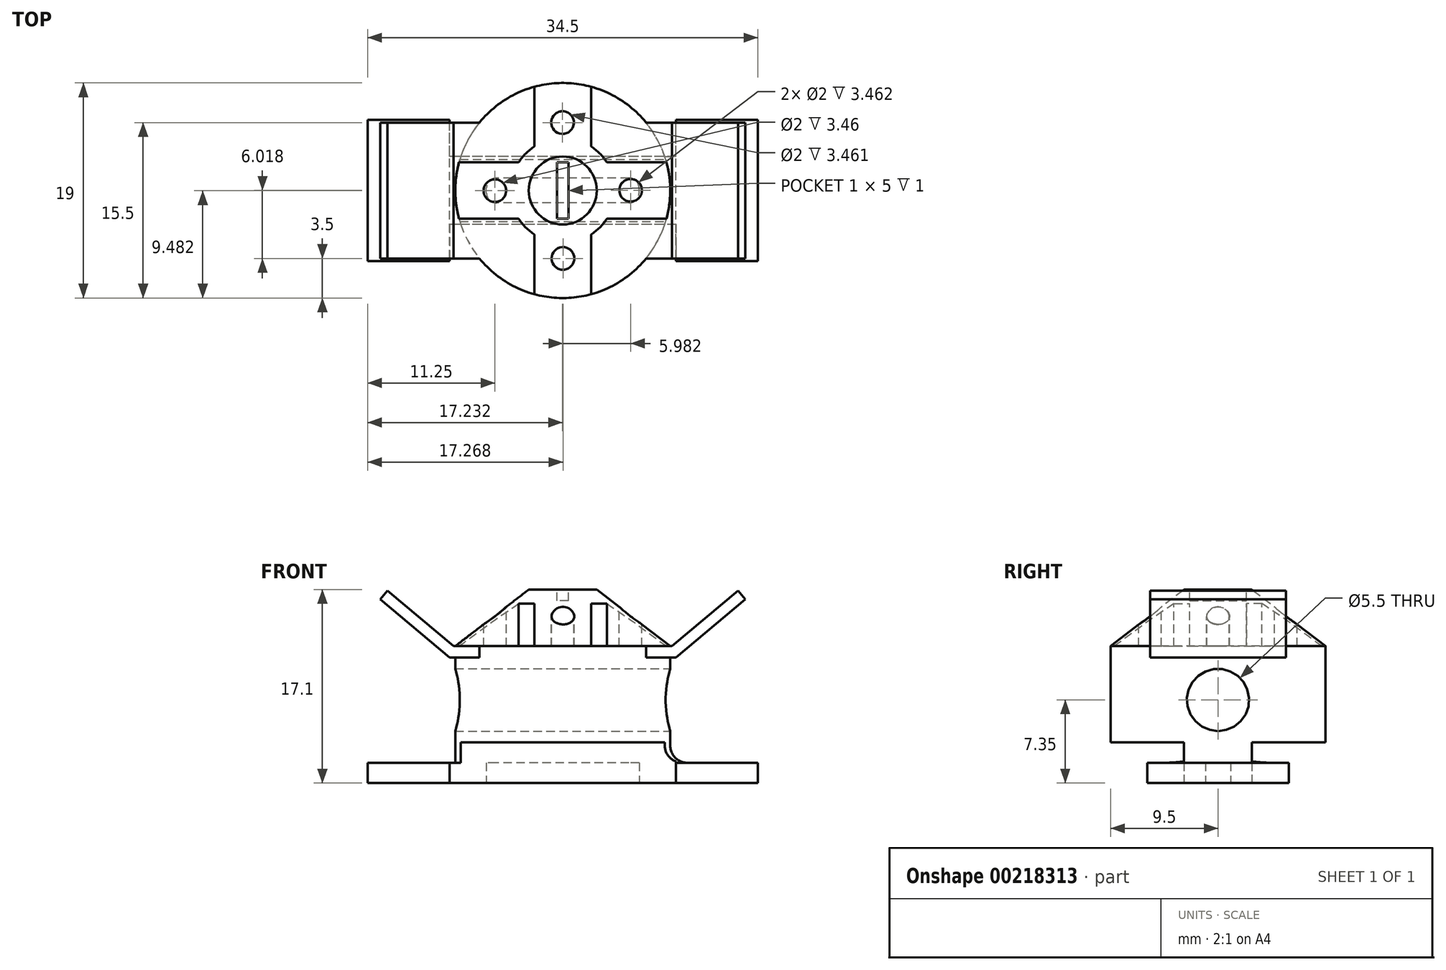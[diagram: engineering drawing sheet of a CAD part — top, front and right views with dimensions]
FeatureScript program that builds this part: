
annotation { "Feature Type Name" : "Feature", "Feature Type Description" : "" }
export const myFeature = defineFeature(function(context is Context, id is Id, definition is map)
    precondition{}
    {
        {
            var Q0;
            Q0=qCreatedBy(makeId("Top.planeOp"),FACE);
            var sketch = newSketch(context, id + "F0", { "sketchPlane" : qUnion([Q0])});
            skLineSegment(sketch, "E0.bottom", {"start": v(17.25, -6.25) * mm, "end": v(10, -6.25) * mm});
            skLineSegment(sketch, "E0.top", {"start": v(17.25, 6.25) * mm, "end": v(10, 6.25) * mm});
            skLineSegment(sketch, "E0.left", {"start": v(17.25, -6.25) * mm, "end": v(17.25, 6.25) * mm});
            skLineSegment(sketch, "E0.right", {"start": v(-17.25, -6.25) * mm, "end": v(-17.25, 6.25) * mm});
            skPoint(sketch, "E0.middle", {"position": v(0, 0) * mm});
            skLineSegment(sketch, "E1.bottom", {"start": v(10, -3) * mm, "end": v(-10, -3) * mm});
            skLineSegment(sketch, "E1.top", {"start": v(10, 3) * mm, "end": v(-10, 3) * mm});
            skLineSegment(sketch, "E2", {"start": v(-10, 3) * mm, "end": v(-10, 6.25) * mm});
            skLineSegment(sketch, "E3", {"start": v(-10, -3) * mm, "end": v(-10, -6.25) * mm});
            skLineSegment(sketch, "E4", {"start": v(10, 3) * mm, "end": v(10, 6.25) * mm});
            skLineSegment(sketch, "E5", {"start": v(10, -3) * mm, "end": v(10, -6.25) * mm});
            skLineSegment(sketch, "E6.trimOffspring", {"start": v(-10, 6.25) * mm, "end": v(-17.25, 6.25) * mm});
            skLineSegment(sketch, "E7.trimOffspring", {"start": v(-10, -6.25) * mm, "end": v(-17.25, -6.25) * mm});
            skLineSegment(sketch, "E8.bottom", {"start": v(5.85, -1.1) * mm, "end": v(-5.85, -1.1) * mm});
            skLineSegment(sketch, "E8.top", {"start": v(5.85, 1.1) * mm, "end": v(-5.85, 1.1) * mm});
            skLineSegment(sketch, "E8.left", {"start": v(6.75, -0.2) * mm, "end": v(6.75, 0.2) * mm});
            skLineSegment(sketch, "E8.right", {"start": v(-6.75, -0.2) * mm, "end": v(-6.75, 0.2) * mm});
            skPoint(sketch, "E9.visualSharp", {"position": v(-6.75, 1.1) * mm});
            skArc(sketch, "E9.filletArc", {"start": v(-5.85, 1.1) * mm, "mid": v(-6.49, 0.84) * mm, "end": v(-6.75, 0.2) * mm});
            skPoint(sketch, "E10.visualSharp", {"position": v(-6.75, -1.1) * mm});
            skArc(sketch, "E10.filletArc", {"start": v(-6.75, -0.2) * mm, "mid": v(-6.49, -0.84) * mm, "end": v(-5.85, -1.1) * mm});
            skPoint(sketch, "E11.visualSharp", {"position": v(6.75, 1.1) * mm});
            skArc(sketch, "E11.filletArc", {"start": v(6.75, 0.2) * mm, "mid": v(6.49, 0.84) * mm, "end": v(5.85, 1.1) * mm});
            skPoint(sketch, "E12.visualSharp", {"position": v(6.75, -1.1) * mm});
            skArc(sketch, "E12.filletArc", {"start": v(5.85, -1.1) * mm, "mid": v(6.49, -0.84) * mm, "end": v(6.75, -0.2) * mm});
            skLineSegment(sketch, "E13", {"start": v(-10, 3) * mm, "end": v(-10, -3) * mm});
            skLineSegment(sketch, "E14", {"start": v(10, 3) * mm, "end": v(10, -3) * mm});
            skSolve(sketch);
        }
        {
            var Q0;
            Q0 = qSketchRegion(id + "F0", true);
            extrude(context, id + "F1", {"entities" : qUnion([Q0]), "depth" : 1.8 * mm});
        }
        {
            var Q0;
            Q0=makeQuery(id+"F1.opExtrude","CAP_FACE",FACE,{"disambiguationData":[OSD([sQuery(id+"F0.wireOp",EDGE,"E0.bottom"),sQuery(id+"F0.wireOp",EDGE,"E0.top"),sQuery(id+"F0.wireOp",EDGE,"E0.left"),sQuery(id+"F0.wireOp",EDGE,"E0.right"),sQuery(id+"F0.wireOp",EDGE,"E1.bottom"),sQuery(id+"F0.wireOp",EDGE,"E1.top"),sQuery(id+"F0.wireOp",EDGE,"E2"),sQuery(id+"F0.wireOp",EDGE,"E3"),sQuery(id+"F0.wireOp",EDGE,"E4"),sQuery(id+"F0.wireOp",EDGE,"E5"),sQuery(id+"F0.wireOp",EDGE,"E6.trimOffspring"),sQuery(id+"F0.wireOp",EDGE,"E7.trimOffspring"),sQuery(id+"F0.wireOp",EDGE,"E8.bottom"),sQuery(id+"F0.wireOp",EDGE,"E8.top"),sQuery(id+"F0.wireOp",EDGE,"E9.filletArc"),sQuery(id+"F0.wireOp",EDGE,"E10.filletArc"),sQuery(id+"F0.wireOp",EDGE,"E11.filletArc"),sQuery(id+"F0.wireOp",EDGE,"E12.filletArc")])],"isStart":false});
            var sketch = newSketch(context, id + "F2", { "sketchPlane" : qUnion([Q0])});
            skPoint(sketch, "E15.middle", {"position": v(0, 0) * mm});
            skLineSegment(sketch, "E16.bottom", {"start": v(9.01, -3) * mm, "end": v(-9.01, -3) * mm});
            skLineSegment(sketch, "E16.top", {"start": v(9.01, 3) * mm, "end": v(-9.01, 3) * mm});
            skArc(sketch, "E17", {"start": v(-9.01, 3) * mm, "mid": v(-9.5, 0) * mm, "end": v(-9.01, -3) * mm});
            skPoint(sketch, "E18", {"position": v(-9.01, 3) * mm});
            skPoint(sketch, "E19", {"position": v(-9.01, -3) * mm});
            skPoint(sketch, "E20", {"position": v(9.01, -3) * mm});
            skPoint(sketch, "E21", {"position": v(9.01, 3) * mm});
            skPoint(sketch, "E16.right.end.orphan", {"position": v(-10, 3) * mm});
            skPoint(sketch, "E22.orphan", {"position": v(-10, -3) * mm});
            skArc(sketch, "E23.trimOffspring", {"start": v(9.01, -3) * mm, "mid": v(9.5, 0) * mm, "end": v(9.01, 3) * mm});
            skPoint(sketch, "E16.left.end.orphan", {"position": v(10, 3) * mm});
            skPoint(sketch, "E24.orphan", {"position": v(10, -3) * mm});
            skSolve(sketch);
        }
        {
            var Q0;
            Q0 = qSketchRegion(id + "F2", true);
            extrude(context, id + "F3", {"entities" : qUnion([Q0]), "operationType" : NewBodyOperationType.ADD, "depth" : 1.8 * mm});
        }
        {
            var Q0;
            Q0=makeQuery(id+"F3.opExtrude","CAP_EDGE",EDGE,{"disambiguationData":[OSD([sQuery(id+"F2.wireOp",EDGE,"E17")])],"isStart":true});
            var Q1;
            Q1=makeQuery(id+"F3.opExtrude","CAP_EDGE",EDGE,{"disambiguationData":[OSD([sQuery(id+"F2.wireOp",EDGE,"E23.trimOffspring")])],"isStart":true});
            fillet(context, id + "F4", {"entities" : qUnion([Q0, Q1]), "radius" : 1.5 * mm, "tangentPropagation" : true, "allowEdgeOverflow" : false});
        }
        {
            var Q0;
            Q0=makeQuery(id+"F3.opExtrude","CAP_FACE",FACE,{"disambiguationData":[OSD([sQuery(id+"F2.wireOp",EDGE,"E16.bottom"),sQuery(id+"F2.wireOp",EDGE,"E16.top"),sQuery(id+"F2.wireOp",EDGE,"E17"),sQuery(id+"F2.wireOp",EDGE,"E23.trimOffspring")])],"isStart":false});
            var sketch = newSketch(context, id + "F5", { "sketchPlane" : qUnion([Q0])});
            skCircle(sketch, "E25", {"center": v(0, 0) * mm, "radius": 9.5 * mm});
            skSolve(sketch);
        }
        {
            var Q0;
            Q0 = qSketchRegion(id + "F5", true);
            extrude(context, id + "F6", {"entities" : qUnion([Q0]), "operationType" : NewBodyOperationType.ADD, "depth" : 8.5 * mm});
        }
        {
            var Q0;
            Q0=makeQuery(id+"F6.opExtrude","CAP_FACE",FACE,{"disambiguationData":[OSD([sQuery(id+"F5.wireOp",EDGE,"E25")])],"isStart":false});
            var sketch = newSketch(context, id + "F7", { "sketchPlane" : qUnion([Q0])});
            skLineSegment(sketch, "E26.bottom", {"start": v(10, -6) * mm, "end": v(-10, -6) * mm});
            skLineSegment(sketch, "E26.top", {"start": v(10, 6) * mm, "end": v(-10, 6) * mm});
            skLineSegment(sketch, "E26.left", {"start": v(10, -6) * mm, "end": v(10, 6) * mm});
            skLineSegment(sketch, "E26.right", {"start": v(-10, -6) * mm, "end": v(-10, 6) * mm});
            skPoint(sketch, "E26.middle", {"position": v(0, 0) * mm});
            skPoint(sketch, "E27", {"position": v(-10, 6) * mm});
            skPoint(sketch, "E28", {"position": v(-10, -6) * mm});
            skPoint(sketch, "E29", {"position": v(10, -6) * mm});
            skPoint(sketch, "E30", {"position": v(10, 6) * mm});
            skLineSegment(sketch, "E31", {"start": v(0, 11) * mm, "end": v(0, -11.61) * mm, "construction": true});
            skPoint(sketch, "E31.startSnap0", {"position": v(0, 6) * mm});
            skSolve(sketch);
        }
        {
            var Q0;
            Q0 = qSketchRegion(id + "F7", true);
            extrude(context, id + "F8", {"entities" : qUnion([Q0]), "operationType" : NewBodyOperationType.ADD, "oppositeDirection" : true, "depth" : 1 * mm});
        }
        {
            var Q0;
            {var subQ0=sQuery(id+"F7.wireOp",EDGE,"E26.bottom");var subQ1=sQuery(id+"F7.wireOp",EDGE,"E26.right");Q0=makeQuery(id+"F8.boolean.opBoolean","SPLIT",EDGE,{"disambiguationData":[TD([makeQuery(id+"F8.opExtrude","SWEPT_FACE",FACE,{"disambiguationData":[OSD([subQ0])]})])],"derivedFrom":makeQuery(id+"F8.opExtrude","CAP_EDGE",EDGE,{"disambiguationData":[OSD([subQ1])],"isStart":false})});}
            cPlane(context, id + "F9", {"entities" : qUnion([Q0]), "cplaneType" : CPlaneType.LINE_ANGLE, "offset" : 25 * mm, "angle" : 40 * degree, "width" : 150 * mm, "height" : 150 * mm});
        }
        {
            var Q0;
            Q0=qCreatedBy(id+"F9.planeOp",FACE);
            var sketch = newSketch(context, id + "F10", { "sketchPlane" : qUnion([Q0])});
            skLineSegment(sketch, "E32.bottom", {"start": v(-14.8, 6) * mm, "end": v(-22.8, 6) * mm});
            skLineSegment(sketch, "E32.top", {"start": v(-14.8, -6) * mm, "end": v(-22.8, -6) * mm});
            skLineSegment(sketch, "E32.left", {"start": v(-14.8, 6) * mm, "end": v(-14.8, -6) * mm});
            skLineSegment(sketch, "E32.right", {"start": v(-22.8, 6) * mm, "end": v(-22.8, -6) * mm});
            skLineSegment(sketch, "E33.bottom", {"start": v(-14.8, 6) * mm, "end": v(-13.8, 6) * mm});
            skLineSegment(sketch, "E33.top", {"start": v(-14.8, -6) * mm, "end": v(-13.8, -6) * mm});
            skLineSegment(sketch, "E33.right", {"start": v(-13.8, 6) * mm, "end": v(-13.8, -6) * mm});
            skSolve(sketch);
        }
        {
            var Q0;
            Q0=makeQuery(id+"F10.imprint","IMPRINT",FACE,{"disambiguationData":[TD([[makeQuery(id+"F10.imprint","IMPRINT",EDGE,{"derivedFrom":sQuery(id+"F10.wireOp",EDGE,"E32.bottom")}),1.0]])]});
            extrude(context, id + "F11", {"entities" : qUnion([Q0]), "depth" : 1 * mm});
        }
        {
            var Q0;
            Q0=makeQuery(id+"F11.opExtrude","SWEPT_BODY",BODY,{"disambiguationData":[OSD([sQuery(id+"F10.wireOp",EDGE,"E32.bottom"),sQuery(id+"F10.wireOp",EDGE,"E32.top"),sQuery(id+"F10.wireOp",EDGE,"E32.right"),sQuery(id+"F10.wireOp",EDGE,"E32.left")])]});
            var Q1;
            Q1=qCreatedBy(makeId("Right.planeOp"),FACE);
            mirror(context, id + "F12", {"operationType" : NewBodyOperationType.ADD, "entities" : qUnion([Q0]), "mirrorPlane" : qUnion([Q1])});
        }
        {
            var Q0;
            Q0=qCreatedBy(makeId("Front.planeOp"),FACE);
            var sketch = newSketch(context, id + "F13", { "sketchPlane" : qUnion([Q0])});
            skLineSegment(sketch, "E34", {"start": v(0, 12.1) * mm, "end": v(0, 17.1) * mm});
            skLineSegment(sketch, "E35", {"start": v(0, 17.1) * mm, "end": v(-3, 17.1) * mm});
            skLineSegment(sketch, "E36", {"start": v(-3, 17.1) * mm, "end": v(-9.5, 12.1) * mm});
            skLineSegment(sketch, "E37", {"start": v(-9.5, 12.1) * mm, "end": v(0, 12.1) * mm});
            skSolve(sketch);
        }
        {
            var Q0;
            Q0 = qSketchRegion(id + "F13", true);
            var Q1;
            Q1=sQuery(id+"F13.wireOp",EDGE,"E34");
            revolve(context, id + "F14", {"operationType" : NewBodyOperationType.ADD, "entities" : qUnion([Q0]), "axis" : qUnion([Q1]), "revolveType" : RevolveType.FULL});
        }
        {
            var Q0;
            Q0=makeQuery(id+"F14.opRevolve","SWEPT_FACE",FACE,{"disambiguationData":[OSD([sQuery(id+"F13.wireOp",EDGE,"E35")])]});
            var sketch = newSketch(context, id + "F15", { "sketchPlane" : qUnion([Q0])});
            skArc(sketch, "E38", {"start": v(-2.5, 3.9) * mm, "mid": v(-3.27, 3.27) * mm, "end": v(-3.9, 2.5) * mm});
            skArc(sketch, "E39", {"start": v(-2.5, 9.17) * mm, "mid": v(-6.72, 6.72) * mm, "end": v(-9.17, 2.5) * mm});
            skLineSegment(sketch, "E40.left", {"start": v(2.5, -9.17) * mm, "end": v(2.5, -3.9) * mm});
            skLineSegment(sketch, "E40.right", {"start": v(-2.5, -9.5) * mm, "end": v(-2.5, -3.9) * mm});
            skLineSegment(sketch, "E41.bottom", {"start": v(9.17, -2.5) * mm, "end": v(3.9, -2.5) * mm});
            skLineSegment(sketch, "E41.top", {"start": v(9.17, 2.5) * mm, "end": v(3.9, 2.5) * mm});
            skLineSegment(sketch, "E42.trimOffspring", {"start": v(-2.5, 3.9) * mm, "end": v(-2.5, 9.17) * mm});
            skLineSegment(sketch, "E43.trimOffspring", {"start": v(-3.9, 2.5) * mm, "end": v(-9.17, 2.5) * mm});
            skArc(sketch, "E44.trimOffspring", {"start": v(-9.17, -2.5) * mm, "mid": v(-6.72, -6.72) * mm, "end": v(-2.5, -9.17) * mm});
            skPoint(sketch, "E45.orphan", {"position": v(-2.5, 9.5) * mm});
            skPoint(sketch, "E46.orphan", {"position": v(2.5, 9.5) * mm});
            skPoint(sketch, "E47.orphan", {"position": v(-9.5, 2.5) * mm});
            skPoint(sketch, "E48.orphan", {"position": v(-9.5, -2.5) * mm});
            skLineSegment(sketch, "E49.trimOffspring", {"start": v(-3.9, -2.5) * mm, "end": v(-9.17, -2.5) * mm});
            skArc(sketch, "E50.trimOffspring", {"start": v(-3.9, -2.5) * mm, "mid": v(-3.27, -3.27) * mm, "end": v(-2.5, -3.9) * mm});
            skLineSegment(sketch, "E51.trimOffspring", {"start": v(2.5, 3.9) * mm, "end": v(2.5, 9.17) * mm});
            skArc(sketch, "E52.trimOffspring", {"start": v(2.5, -3.9) * mm, "mid": v(3.27, -3.27) * mm, "end": v(3.9, -2.5) * mm});
            skArc(sketch, "E53.trimOffspring", {"start": v(3.9, 2.5) * mm, "mid": v(3.27, 3.27) * mm, "end": v(2.5, 3.9) * mm});
            skArc(sketch, "E54.trimOffspring", {"start": v(2.5, -9.17) * mm, "mid": v(6.72, -6.72) * mm, "end": v(9.17, -2.5) * mm});
            skPoint(sketch, "E55.orphan", {"position": v(2.5, -9.5) * mm});
            skPoint(sketch, "E56.orphan", {"position": v(9.5, 2.5) * mm});
            skArc(sketch, "E57.trimOffspring", {"start": v(9.17, 2.5) * mm, "mid": v(6.72, 6.72) * mm, "end": v(2.5, 9.17) * mm});
            skPoint(sketch, "E58.orphan", {"position": v(9.5, -2.5) * mm});
            skCircle(sketch, "E59", {"center": v(0, 0) * mm, "radius": 6 * mm, "construction": true});
            skLineSegment(sketch, "E60", {"start": v(-10.51, 0) * mm, "end": v(10.47, 0) * mm, "construction": true});
            skLineSegment(sketch, "E61", {"start": v(-0.02, -9.48) * mm, "end": v(-0.02, 7.04) * mm, "construction": true});
            skPoint(sketch, "E61.startSnap0", {"position": v(-0.02, 0) * mm});
            skPoint(sketch, "E62", {"position": v(-0.02, 6) * mm});
            skCircle(sketch, "E63", {"center": v(-0.02, 6) * mm, "radius": 1 * mm});
            skCircle(sketch, "E64.1.0", {"center": v(-6, -0.02) * mm, "radius": 1 * mm});
            skCircle(sketch, "E64.2.0", {"center": v(0.02, -6) * mm, "radius": 1 * mm});
            skCircle(sketch, "E64.3.0", {"center": v(6, 0.02) * mm, "radius": 1 * mm});
            skSolve(sketch);
        }
        {
            var Q0;
            Q0 = qSketchRegion(id + "F15", true);
            extrude(context, id + "F16", {"entities" : qUnion([Q0]), "operationType" : NewBodyOperationType.REMOVE, "oppositeDirection" : true, "depth" : 5 * mm});
        }
        {
            var Q0;
            Q0=makeQuery(id+"F14.opRevolve","SWEPT_FACE",FACE,{"disambiguationData":[OSD([sQuery(id+"F13.wireOp",EDGE,"E35")])]});
            var sketch = newSketch(context, id + "F17", { "sketchPlane" : qUnion([Q0])});
            skLineSegment(sketch, "E65.bottom", {"start": v(0.5, -2.5) * mm, "end": v(-0.5, -2.5) * mm});
            skLineSegment(sketch, "E65.top", {"start": v(0.5, 2.5) * mm, "end": v(-0.5, 2.5) * mm});
            skLineSegment(sketch, "E65.left", {"start": v(0.5, -2.5) * mm, "end": v(0.5, 2.5) * mm});
            skLineSegment(sketch, "E65.right", {"start": v(-0.5, -2.5) * mm, "end": v(-0.5, 2.5) * mm});
            skPoint(sketch, "E65.middle", {"position": v(0, 0) * mm});
            skSolve(sketch);
        }
        {
            var Q0;
            Q0 = qSketchRegion(id + "F17", true);
            extrude(context, id + "F18", {"entities" : qUnion([Q0]), "operationType" : NewBodyOperationType.REMOVE, "oppositeDirection" : true, "depth" : 1 * mm});
        }
        {
            var Q0;
            Q0=qCreatedBy(makeId("Right.planeOp"),FACE);
            cPlane(context, id + "F19", {"entities" : qUnion([Q0]), "cplaneType" : CPlaneType.OFFSET, "offset" : 20 * mm, "width" : 150 * mm, "height" : 150 * mm});
        }
        {
            var Q0;
            Q0=qCreatedBy(id+"F19.planeOp",FACE);
            var sketch = newSketch(context, id + "F20", { "sketchPlane" : qUnion([Q0])});
            skLineSegment(sketch, "E66", {"start": v(0, 0) * mm, "end": v(0, 22.9) * mm, "construction": true});
            skPoint(sketch, "E67", {"position": v(0, 3.6) * mm});
            skPoint(sketch, "E68", {"position": v(0, 11.1) * mm});
            skPoint(sketch, "E69", {"position": v(0, 7.35) * mm});
            skSolve(sketch);
        }
        {
            var Q0;
            Q0=sQuery(id+"F20.wireOp",VERTEX,"E69");
            var Q1;
            Q1=makeQuery(id+"F1.opExtrude","SWEPT_BODY",BODY,{"disambiguationData":[OSD([sQuery(id+"F0.wireOp",EDGE,"E0.bottom"),sQuery(id+"F0.wireOp",EDGE,"E0.top"),sQuery(id+"F0.wireOp",EDGE,"E0.left"),sQuery(id+"F0.wireOp",EDGE,"E0.right"),sQuery(id+"F0.wireOp",EDGE,"E1.bottom"),sQuery(id+"F0.wireOp",EDGE,"E1.top"),sQuery(id+"F0.wireOp",EDGE,"E2"),sQuery(id+"F0.wireOp",EDGE,"E3"),sQuery(id+"F0.wireOp",EDGE,"E4"),sQuery(id+"F0.wireOp",EDGE,"E5"),sQuery(id+"F0.wireOp",EDGE,"E6.trimOffspring"),sQuery(id+"F0.wireOp",EDGE,"E7.trimOffspring"),sQuery(id+"F0.wireOp",EDGE,"E8.bottom"),sQuery(id+"F0.wireOp",EDGE,"E8.top"),sQuery(id+"F0.wireOp",EDGE,"E9.filletArc"),sQuery(id+"F0.wireOp",EDGE,"E10.filletArc"),sQuery(id+"F0.wireOp",EDGE,"E11.filletArc"),sQuery(id+"F0.wireOp",EDGE,"E12.filletArc")])]});
            hole(context, id + "F21", {"style" : HoleStyle.SIMPLE, "endStyle" : HoleEndStyle.THROUGH, "standardTappedOrClearance" : lookupTablePath({ "standard" : "ISO", "fit" : "Normal", "size" : "M5", "type" : "Clearance" }), "standardBlindInLast" : lookupTablePath({ "fit" : "Standard", "standard" : "ISO", "size" : "M5", "type" : "Clearance" }), "holeDiameter" : 5.5 * mm, "tappedDepth" : 12 * mm, "tapClearance" : 3, "locations" : qUnion([Q0]), "scope" : qUnion([Q1])});
        }
    });
